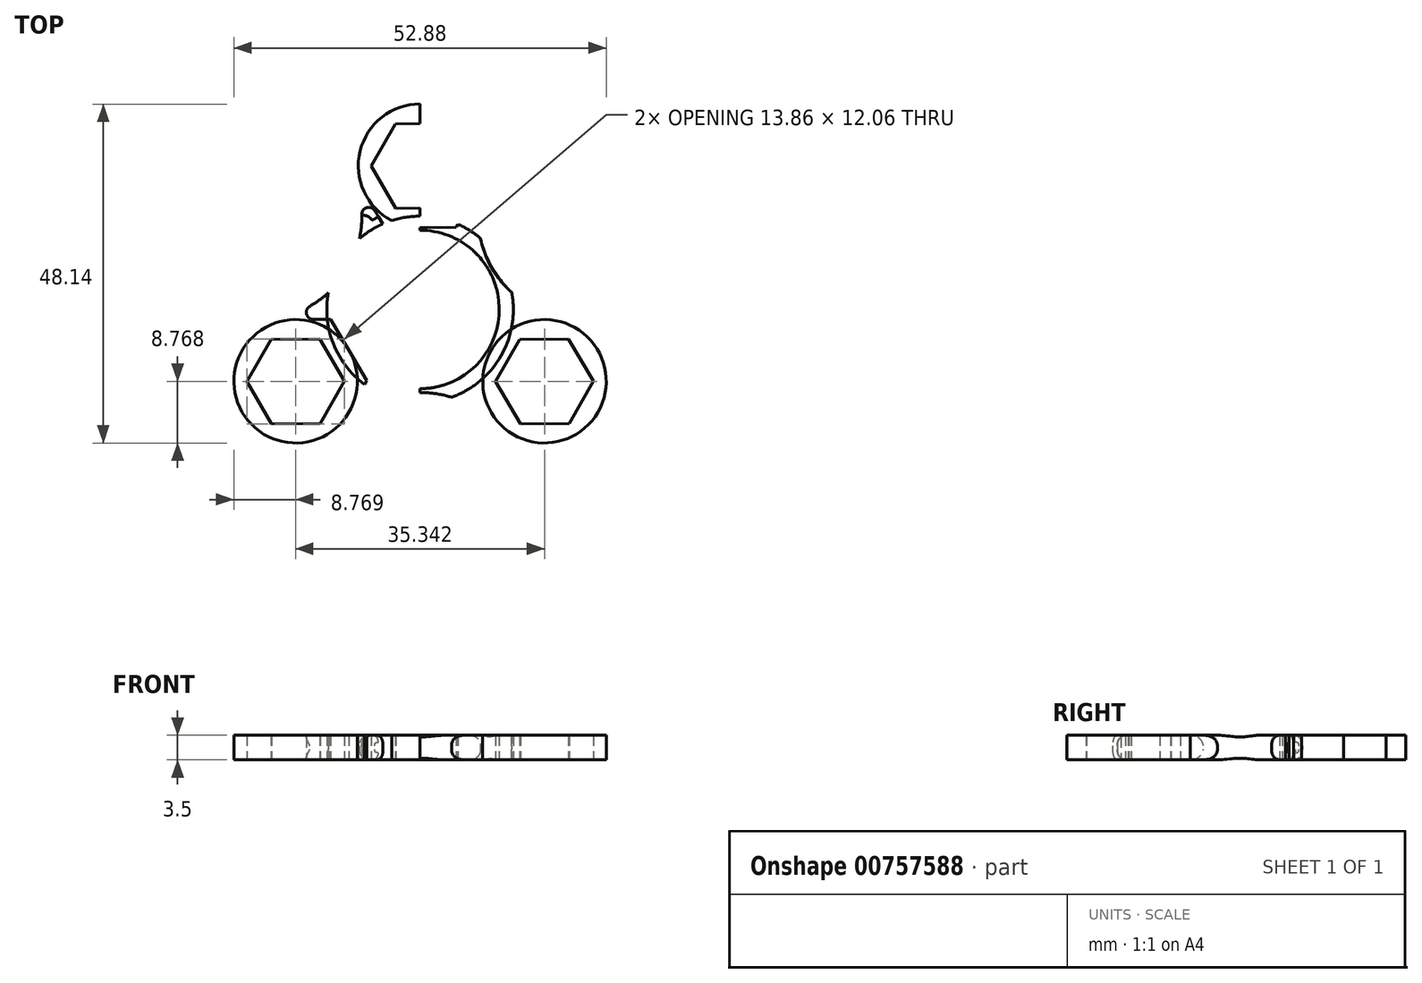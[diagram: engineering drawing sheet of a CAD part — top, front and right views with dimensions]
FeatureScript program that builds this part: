
annotation { "Feature Type Name" : "Feature", "Feature Type Description" : "" }
export const myFeature = defineFeature(function(context is Context, id is Id, definition is map)
    precondition{}
    {
        {
            var Q0;
            Q0=qCreatedBy(makeId("Top.planeOp"),FACE);
            var sketch = newSketch(context, id + "F0", { "sketchPlane" : qUnion([Q0])});
            skCircle(sketch, "E0", {"center": v(0, 0) * mm, "radius": 11.25 * mm});
            skCircle(sketch, "E1", {"center": v(0, 0) * mm, "radius": 13.25 * mm});
            skCircle(sketch, "E2.cCircle", {"center": v(0, 20.4) * mm, "radius": 6 * mm});
            skLineSegment(sketch, "E2.0", {"start": v(-3.52, 26.37) * mm, "end": v(3.41, 26.43) * mm});
            skLineSegment(sketch, "E2.1", {"start": v(3.41, 26.43) * mm, "end": v(6.93, 20.46) * mm});
            skLineSegment(sketch, "E2.2", {"start": v(6.93, 20.46) * mm, "end": v(3.52, 14.43) * mm});
            skLineSegment(sketch, "E2.3", {"start": v(3.52, 14.43) * mm, "end": v(-3.41, 14.38) * mm});
            skLineSegment(sketch, "E2.4", {"start": v(-3.41, 14.38) * mm, "end": v(-6.93, 20.35) * mm});
            skLineSegment(sketch, "E2.5", {"start": v(-6.93, 20.35) * mm, "end": v(-3.52, 26.37) * mm});
            skPoint(sketch, "E2.0.midPoint", {"position": v(-0.05, 26.4) * mm});
            skLineSegment(sketch, "E3", {"start": v(0, 35.27) * mm, "end": v(0, -24.23) * mm});
            skCircle(sketch, "E4.cCircle", {"center": v(0, 20.4) * mm, "radius": 8.77 * mm});
            skLineSegment(sketch, "E4.0", {"start": v(4.99, 29.21) * mm, "end": v(10.12, 20.5) * mm});
            skLineSegment(sketch, "E4.1", {"start": v(10.12, 20.5) * mm, "end": v(5.14, 11.68) * mm});
            skLineSegment(sketch, "E4.2", {"start": v(5.14, 11.68) * mm, "end": v(-4.99, 11.6) * mm});
            skLineSegment(sketch, "E4.3", {"start": v(-4.99, 11.6) * mm, "end": v(-10.12, 20.32) * mm});
            skLineSegment(sketch, "E4.4", {"start": v(-10.12, 20.32) * mm, "end": v(-5.14, 29.13) * mm});
            skLineSegment(sketch, "E4.5", {"start": v(-5.14, 29.13) * mm, "end": v(4.99, 29.21) * mm});
            skPoint(sketch, "E4.0.midPoint", {"position": v(7.56, 24.85) * mm});
            skCircle(sketch, "E5.1.0", {"center": v(-17.67, -10.2) * mm, "radius": 8.77 * mm});
            skCircle(sketch, "E5.1.1", {"center": v(-17.67, -10.2) * mm, "radius": 6 * mm});
            skLineSegment(sketch, "E5.1.2", {"start": v(-21.19, -4.23) * mm, "end": v(-14.26, -4.17) * mm});
            skPoint(sketch, "E5.1.3", {"position": v(-22.84, -13.25) * mm});
            skPoint(sketch, "E5.1.6", {"position": v(-25.3, -5.88) * mm});
            skLineSegment(sketch, "E5.1.7", {"start": v(-7.55, -10.12) * mm, "end": v(-12.53, -18.93) * mm});
            skLineSegment(sketch, "E5.1.8", {"start": v(-12.68, -1.4) * mm, "end": v(-7.55, -10.12) * mm});
            skLineSegment(sketch, "E5.1.9", {"start": v(-14.26, -4.17) * mm, "end": v(-10.74, -10.14) * mm});
            skLineSegment(sketch, "E5.1.10", {"start": v(-10.74, -10.14) * mm, "end": v(-14.16, -16.17) * mm});
            skLineSegment(sketch, "E5.1.11", {"start": v(-22.8, -1.48) * mm, "end": v(-12.68, -1.4) * mm});
            skLineSegment(sketch, "E5.1.12", {"start": v(-22.66, -19.01) * mm, "end": v(-27.8, -10.29) * mm});
            skLineSegment(sketch, "E5.1.13", {"start": v(-21.08, -16.23) * mm, "end": v(-24.6, -10.26) * mm});
            skLineSegment(sketch, "E5.1.14", {"start": v(-24.6, -10.26) * mm, "end": v(-21.19, -4.23) * mm});
            skLineSegment(sketch, "E5.1.15", {"start": v(-14.16, -16.17) * mm, "end": v(-21.08, -16.23) * mm});
            skCircle(sketch, "E5.2.0", {"center": v(17.67, -10.2) * mm, "radius": 8.77 * mm});
            skCircle(sketch, "E5.2.1", {"center": v(17.67, -10.2) * mm, "radius": 6 * mm});
            skLineSegment(sketch, "E5.2.2", {"start": v(14.26, -16.23) * mm, "end": v(10.74, -10.26) * mm});
            skPoint(sketch, "E5.2.3", {"position": v(22.9, -13.16) * mm});
            skPoint(sketch, "E5.2.6", {"position": v(17.75, -18.97) * mm});
            skLineSegment(sketch, "E5.2.7", {"start": v(12.53, -1.48) * mm, "end": v(22.66, -1.4) * mm});
            skLineSegment(sketch, "E5.2.8", {"start": v(7.55, -10.29) * mm, "end": v(12.53, -1.48) * mm});
            skLineSegment(sketch, "E5.2.9", {"start": v(10.74, -10.26) * mm, "end": v(14.16, -4.23) * mm});
            skLineSegment(sketch, "E5.2.10", {"start": v(14.16, -4.23) * mm, "end": v(21.08, -4.17) * mm});
            skLineSegment(sketch, "E5.2.11", {"start": v(12.68, -19.01) * mm, "end": v(7.55, -10.29) * mm});
            skLineSegment(sketch, "E5.2.12", {"start": v(27.8, -10.12) * mm, "end": v(22.8, -18.93) * mm});
            skLineSegment(sketch, "E5.2.13", {"start": v(24.6, -10.14) * mm, "end": v(21.19, -16.17) * mm});
            skLineSegment(sketch, "E5.2.14", {"start": v(21.19, -16.17) * mm, "end": v(14.26, -16.23) * mm});
            skLineSegment(sketch, "E5.2.15", {"start": v(21.08, -4.17) * mm, "end": v(24.6, -10.14) * mm});
            skLineSegment(sketch, "E6", {"start": v(-12.53, -18.93) * mm, "end": v(-22.66, -19.01) * mm});
            skLineSegment(sketch, "E7", {"start": v(-27.8, -10.29) * mm, "end": v(-22.8, -1.48) * mm});
            skLineSegment(sketch, "E8", {"start": v(12.68, -19.01) * mm, "end": v(22.8, -18.93) * mm});
            skLineSegment(sketch, "E9", {"start": v(27.8, -10.12) * mm, "end": v(22.66, -1.4) * mm});
            skArc(sketch, "E10", {"start": v(12.68, -19.01) * mm, "mid": v(0.1, -11.79) * mm, "end": v(-12.53, -18.93) * mm});
            skArc(sketch, "E11.1.0", {"start": v(10.12, 20.5) * mm, "mid": v(10.16, 5.98) * mm, "end": v(22.66, -1.4) * mm});
            skArc(sketch, "E11.2.0", {"start": v(-22.8, -1.48) * mm, "mid": v(-10.26, 5.8) * mm, "end": v(-10.12, 20.32) * mm});
            skSolve(sketch);
        }
        {
            var Q0;
            Q0=makeQuery(id+"F0.imprint","IMPRINT",FACE,{"disambiguationData":[TD([[makeQuery(id+"F0.imprint","IMPRINT",EDGE,{"derivedFrom":sQuery(id+"F0.wireOp",EDGE,"E5.1.2")}),1.0]])]});
            var Q1;
            {var subQ0=sQuery(id+"F0.wireOp",EDGE,"E11.2.0");var subQ3=sQuery(id+"F0.wireOp",EDGE,"E1");var subQ5=makeQuery(id+"F0.imprint","INTERSECT",VERTEX,{"disambiguationData":[OD(1.0)],"derivedFrom":[subQ3,subQ0]});Q1=makeQuery(id+"F0.imprint","IMPRINT",FACE,{"disambiguationData":[TD([[makeQuery(id+"F0.imprint","IMPRINT",EDGE,{"disambiguationData":[TD([[subQ5,-1.0]])],"derivedFrom":subQ3}),-1.0]])]});}
            var Q2;
            {var subQ15=sQuery(id+"F0.wireOp",EDGE,"E4.2");Q2=makeQuery(id+"F0.imprint","IMPRINT",FACE,{"disambiguationData":[TD([[makeQuery(id+"F0.imprint","IMPRINT",EDGE,{"derivedFrom":subQ15}),1.0]])]});}
            var Q3;
            {var subQ0=sQuery(id+"F0.wireOp",EDGE,"E11.2.0");var subQ3=sQuery(id+"F0.wireOp",EDGE,"E1");var subQ5=makeQuery(id+"F0.imprint","INTERSECT",VERTEX,{"disambiguationData":[OD(0.0)],"derivedFrom":[subQ3,subQ0]});Q3=makeQuery(id+"F0.imprint","IMPRINT",FACE,{"disambiguationData":[TD([[makeQuery(id+"F0.imprint","IMPRINT",EDGE,{"disambiguationData":[TD([[subQ5,1.0]])],"derivedFrom":subQ3}),-1.0]])]});}
            var Q4;
            {var subQ0=sQuery(id+"F0.wireOp",EDGE,"E5.1.8");Q4=makeQuery(id+"F0.imprint","IMPRINT",FACE,{"disambiguationData":[TD([[makeQuery(id+"F0.imprint","IMPRINT",EDGE,{"derivedFrom":subQ0}),-1.0]])]});}
            var Q5;
            {var subQ0=sQuery(id+"F0.wireOp",EDGE,"E10");var subQ3=sQuery(id+"F0.wireOp",EDGE,"E1");var subQ5=makeQuery(id+"F0.imprint","INTERSECT",VERTEX,{"disambiguationData":[OD(1.0)],"derivedFrom":[subQ3,subQ0]});Q5=makeQuery(id+"F0.imprint","IMPRINT",FACE,{"disambiguationData":[TD([[makeQuery(id+"F0.imprint","IMPRINT",EDGE,{"disambiguationData":[TD([[subQ5,1.0]])],"derivedFrom":subQ3}),-1.0]])]});}
            var Q6;
            {var subQ0=sQuery(id+"F0.wireOp",EDGE,"E10");var subQ1=sQuery(id+"F0.wireOp",EDGE,"E1");var subQ2=makeQuery(id+"F0.imprint","INTERSECT",VERTEX,{"disambiguationData":[OD(0.0)],"derivedFrom":[subQ1,subQ0]});Q6=makeQuery(id+"F0.imprint","IMPRINT",FACE,{"disambiguationData":[TD([[makeQuery(id+"F0.imprint","IMPRINT",EDGE,{"disambiguationData":[TD([[subQ2,-1.0]])],"derivedFrom":subQ1}),-1.0]])]});}
            var Q7;
            {var subQ5=sQuery(id+"F0.wireOp",EDGE,"E5.2.8");Q7=makeQuery(id+"F0.imprint","IMPRINT",FACE,{"disambiguationData":[TD([[makeQuery(id+"F0.imprint","IMPRINT",EDGE,{"derivedFrom":subQ5}),-1.0]])]});}
            var Q8;
            Q8=makeQuery(id+"F0.imprint","IMPRINT",FACE,{"disambiguationData":[TD([[makeQuery(id+"F0.imprint","IMPRINT",EDGE,{"derivedFrom":sQuery(id+"F0.wireOp",EDGE,"E5.2.2")}),1.0]])]});
            var Q9;
            {var subQ0=sQuery(id+"F0.wireOp",EDGE,"E11.1.0");var subQ1=sQuery(id+"F0.wireOp",EDGE,"E1");var subQ2=makeQuery(id+"F0.imprint","INTERSECT",VERTEX,{"disambiguationData":[OD(0.0)],"derivedFrom":[subQ1,subQ0]});Q9=makeQuery(id+"F0.imprint","IMPRINT",FACE,{"disambiguationData":[TD([[makeQuery(id+"F0.imprint","IMPRINT",EDGE,{"disambiguationData":[TD([[subQ2,1.0]])],"derivedFrom":subQ1}),-1.0]])]});}
            var Q10;
            {var subQ0=sQuery(id+"F0.wireOp",EDGE,"E11.1.0");var subQ3=sQuery(id+"F0.wireOp",EDGE,"E1");var subQ5=makeQuery(id+"F0.imprint","INTERSECT",VERTEX,{"disambiguationData":[OD(1.0)],"derivedFrom":[subQ3,subQ0]});Q10=makeQuery(id+"F0.imprint","IMPRINT",FACE,{"disambiguationData":[TD([[makeQuery(id+"F0.imprint","IMPRINT",EDGE,{"disambiguationData":[TD([[subQ5,-1.0]])],"derivedFrom":subQ3}),-1.0]])]});}
            var Q11;
            {var subQ0=sQuery(id+"F0.wireOp",EDGE,"E4.2");Q11=makeQuery(id+"F0.imprint","IMPRINT",FACE,{"disambiguationData":[TD([[makeQuery(id+"F0.imprint","IMPRINT",EDGE,{"derivedFrom":subQ0}),-1.0]])]});}
            var Q12;
            Q12=makeQuery(id+"F0.imprint","IMPRINT",FACE,{"disambiguationData":[TD([[makeQuery(id+"F0.imprint","IMPRINT",EDGE,{"derivedFrom":sQuery(id+"F0.wireOp",EDGE,"E2.0")}),1.0]])]});
            extrude(context, id + "F1", {"entities" : qUnion([Q0, Q1, Q2, Q3, Q4, Q5, Q6, Q7, Q8, Q9, Q10, Q11, Q12]), "depth" : 3.5 * mm, "offsetDistance" : 25 * mm});
        }
        {
            var Q0;
            Q0=makeQuery(id+"F1.opExtrude","CAP_EDGE",EDGE,{"disambiguationData":[OSD([sQuery(id+"F0.wireOp",EDGE,"E4.5")])],"isStart":false});
            var Q1;
            Q1=makeQuery(id+"F1.opExtrude","CAP_EDGE",EDGE,{"disambiguationData":[OSD([sQuery(id+"F0.wireOp",EDGE,"E11.2.0")])],"isStart":false});
            var Q2;
            Q2=makeQuery(id+"F1.opExtrude","CAP_EDGE",EDGE,{"disambiguationData":[OSD([sQuery(id+"F0.wireOp",EDGE,"E4.4")])],"isStart":false});
            var Q3;
            Q3=makeQuery(id+"F1.opExtrude","CAP_EDGE",EDGE,{"disambiguationData":[OSD([sQuery(id+"F0.wireOp",EDGE,"E7")])],"isStart":false});
            var Q4;
            Q4=makeQuery(id+"F1.opExtrude","CAP_EDGE",EDGE,{"disambiguationData":[OSD([sQuery(id+"F0.wireOp",EDGE,"E5.1.12")])],"isStart":false});
            var Q5;
            Q5=makeQuery(id+"F1.opExtrude","CAP_EDGE",EDGE,{"disambiguationData":[OSD([sQuery(id+"F0.wireOp",EDGE,"E6")])],"isStart":false});
            var Q6;
            Q6=makeQuery(id+"F1.opExtrude","CAP_EDGE",EDGE,{"disambiguationData":[OSD([sQuery(id+"F0.wireOp",EDGE,"E10")])],"isStart":false});
            var Q7;
            Q7=makeQuery(id+"F1.opExtrude","CAP_EDGE",EDGE,{"disambiguationData":[OSD([sQuery(id+"F0.wireOp",EDGE,"E8")])],"isStart":false});
            var Q8;
            Q8=makeQuery(id+"F1.opExtrude","CAP_EDGE",EDGE,{"disambiguationData":[OSD([sQuery(id+"F0.wireOp",EDGE,"E9")])],"isStart":false});
            var Q9;
            Q9=makeQuery(id+"F1.opExtrude","CAP_EDGE",EDGE,{"disambiguationData":[OSD([sQuery(id+"F0.wireOp",EDGE,"E11.1.0")])],"isStart":false});
            var Q10;
            Q10=makeQuery(id+"F1.opExtrude","CAP_EDGE",EDGE,{"disambiguationData":[OSD([sQuery(id+"F0.wireOp",EDGE,"E6")])],"isStart":true});
            var Q11;
            Q11=makeQuery(id+"F1.opExtrude","CAP_EDGE",EDGE,{"disambiguationData":[OSD([sQuery(id+"F0.wireOp",EDGE,"E10")])],"isStart":true});
            var Q12;
            Q12=makeQuery(id+"F1.opExtrude","CAP_EDGE",EDGE,{"disambiguationData":[OSD([sQuery(id+"F0.wireOp",EDGE,"E5.1.12")])],"isStart":true});
            var Q13;
            Q13=makeQuery(id+"F1.opExtrude","CAP_EDGE",EDGE,{"disambiguationData":[OSD([sQuery(id+"F0.wireOp",EDGE,"E7")])],"isStart":true});
            var Q14;
            Q14=makeQuery(id+"F1.opExtrude","CAP_EDGE",EDGE,{"disambiguationData":[OSD([sQuery(id+"F0.wireOp",EDGE,"E11.2.0")])],"isStart":true});
            var Q15;
            Q15=makeQuery(id+"F1.opExtrude","CAP_EDGE",EDGE,{"disambiguationData":[OSD([sQuery(id+"F0.wireOp",EDGE,"E4.4")])],"isStart":true});
            var Q16;
            Q16=makeQuery(id+"F1.opExtrude","CAP_EDGE",EDGE,{"disambiguationData":[OSD([sQuery(id+"F0.wireOp",EDGE,"E4.5")])],"isStart":true});
            var Q17;
            Q17=makeQuery(id+"F1.opExtrude","CAP_EDGE",EDGE,{"disambiguationData":[OSD([sQuery(id+"F0.wireOp",EDGE,"E4.0")])],"isStart":false});
            var Q18;
            Q18=makeQuery(id+"F1.opExtrude","CAP_EDGE",EDGE,{"disambiguationData":[OSD([sQuery(id+"F0.wireOp",EDGE,"E4.0")])],"isStart":true});
            var Q19;
            Q19=makeQuery(id+"F1.opExtrude","CAP_EDGE",EDGE,{"disambiguationData":[OSD([sQuery(id+"F0.wireOp",EDGE,"E11.1.0")])],"isStart":true});
            var Q20;
            Q20=makeQuery(id+"F1.opExtrude","CAP_EDGE",EDGE,{"disambiguationData":[OSD([sQuery(id+"F0.wireOp",EDGE,"E9")])],"isStart":true});
            var Q21;
            Q21=makeQuery(id+"F1.opExtrude","CAP_EDGE",EDGE,{"disambiguationData":[OSD([sQuery(id+"F0.wireOp",EDGE,"E5.2.12")])],"isStart":true});
            var Q22;
            Q22=makeQuery(id+"F1.opExtrude","CAP_EDGE",EDGE,{"disambiguationData":[OSD([sQuery(id+"F0.wireOp",EDGE,"E8")])],"isStart":true});
            fillet(context, id + "F2", {"entities" : qUnion([Q0, Q1, Q2, Q3, Q4, Q5, Q6, Q7, Q8, Q9, Q10, Q11, Q12, Q13, Q14, Q15, Q16, Q17, Q18, Q19, Q20, Q21, Q22]), "radius" : 1.5 * mm, "tangentPropagation" : true, "rho" : 0.5, "crossSection" : FilletCrossSection.CONIC, "allowEdgeOverflow" : false});
        }
        {
            var Q0;
            Q0=makeQuery(id+"F2.opFillet","BLEND_EDGE",EDGE,{"blendedFrom":[makeQuery(id+"F1.opExtrude","CAP_EDGE",EDGE,{"disambiguationData":[OSD([sQuery(id+"F0.wireOp",EDGE,"E9")])],"isStart":false}),makeQuery(id+"F1.opExtrude","CAP_EDGE",EDGE,{"disambiguationData":[OSD([sQuery(id+"F0.wireOp",EDGE,"E11.1.0")])],"isStart":false})],"blendedInto":[]});
            var Q1;
            Q1=makeQuery(id+"F2.opFillet","BLEND_EDGE",EDGE,{"blendedFrom":[makeQuery(id+"F1.opExtrude","CAP_EDGE",EDGE,{"disambiguationData":[OSD([sQuery(id+"F0.wireOp",EDGE,"E9")])],"isStart":true}),makeQuery(id+"F1.opExtrude","CAP_EDGE",EDGE,{"disambiguationData":[OSD([sQuery(id+"F0.wireOp",EDGE,"E11.1.0")])],"isStart":true})],"blendedInto":[]});
            var Q2;
            Q2=makeQuery(id+"F2.opFillet","BLEND_EDGE",EDGE,{"blendedFrom":[makeQuery(id+"F1.opExtrude","CAP_EDGE",EDGE,{"disambiguationData":[OSD([sQuery(id+"F0.wireOp",EDGE,"E8")])],"isStart":false}),makeQuery(id+"F1.opExtrude","CAP_EDGE",EDGE,{"disambiguationData":[OSD([sQuery(id+"F0.wireOp",EDGE,"E10")])],"isStart":false})],"blendedInto":[]});
            var Q3;
            Q3=makeQuery(id+"F2.opFillet","BLEND_EDGE",EDGE,{"blendedFrom":[makeQuery(id+"F1.opExtrude","CAP_EDGE",EDGE,{"disambiguationData":[OSD([sQuery(id+"F0.wireOp",EDGE,"E8")])],"isStart":true}),makeQuery(id+"F1.opExtrude","CAP_EDGE",EDGE,{"disambiguationData":[OSD([sQuery(id+"F0.wireOp",EDGE,"E10")])],"isStart":true})],"blendedInto":[]});
            var Q4;
            Q4=makeQuery(id+"F1.opExtrude","SWEPT_EDGE",EDGE,{"disambiguationData":[OSD([sQuery(id+"F0.wireOp",EDGE,"E5.2.11"),sQuery(id+"F0.wireOp",EDGE,"E8"),sQuery(id+"F0.wireOp",EDGE,"E10")])]});
            var Q5;
            Q5=makeQuery(id+"F2.opFillet","BLEND_EDGE",EDGE,{"blendedFrom":[makeQuery(id+"F1.opExtrude","CAP_EDGE",EDGE,{"disambiguationData":[OSD([sQuery(id+"F0.wireOp",EDGE,"E6")])],"isStart":false}),makeQuery(id+"F1.opExtrude","CAP_EDGE",EDGE,{"disambiguationData":[OSD([sQuery(id+"F0.wireOp",EDGE,"E10")])],"isStart":false})],"blendedInto":[]});
            var Q6;
            Q6=makeQuery(id+"F1.opExtrude","SWEPT_EDGE",EDGE,{"disambiguationData":[OSD([sQuery(id+"F0.wireOp",EDGE,"E5.1.7"),sQuery(id+"F0.wireOp",EDGE,"E6"),sQuery(id+"F0.wireOp",EDGE,"E10")])]});
            var Q7;
            Q7=makeQuery(id+"F2.opFillet","BLEND_EDGE",EDGE,{"blendedFrom":[makeQuery(id+"F1.opExtrude","CAP_EDGE",EDGE,{"disambiguationData":[OSD([sQuery(id+"F0.wireOp",EDGE,"E6")])],"isStart":true}),makeQuery(id+"F1.opExtrude","CAP_EDGE",EDGE,{"disambiguationData":[OSD([sQuery(id+"F0.wireOp",EDGE,"E10")])],"isStart":true})],"blendedInto":[]});
            var Q8;
            Q8=makeQuery(id+"F2.opFillet","BLEND_EDGE",EDGE,{"blendedFrom":[makeQuery(id+"F1.opExtrude","CAP_EDGE",EDGE,{"disambiguationData":[OSD([sQuery(id+"F0.wireOp",EDGE,"E5.1.12")])],"isStart":false}),makeQuery(id+"F1.opExtrude","CAP_EDGE",EDGE,{"disambiguationData":[OSD([sQuery(id+"F0.wireOp",EDGE,"E6")])],"isStart":false})],"blendedInto":[]});
            var Q9;
            Q9=makeQuery(id+"F1.opExtrude","SWEPT_EDGE",EDGE,{"disambiguationData":[OSD([sQuery(id+"F0.wireOp",EDGE,"E5.1.12"),sQuery(id+"F0.wireOp",EDGE,"E6")])]});
            var Q10;
            Q10=makeQuery(id+"F2.opFillet","BLEND_EDGE",EDGE,{"blendedFrom":[makeQuery(id+"F1.opExtrude","CAP_EDGE",EDGE,{"disambiguationData":[OSD([sQuery(id+"F0.wireOp",EDGE,"E5.1.12")])],"isStart":true}),makeQuery(id+"F1.opExtrude","CAP_EDGE",EDGE,{"disambiguationData":[OSD([sQuery(id+"F0.wireOp",EDGE,"E6")])],"isStart":true})],"blendedInto":[]});
            var Q11;
            Q11=makeQuery(id+"F2.opFillet","BLEND_EDGE",EDGE,{"blendedFrom":[makeQuery(id+"F1.opExtrude","CAP_EDGE",EDGE,{"disambiguationData":[OSD([sQuery(id+"F0.wireOp",EDGE,"E5.1.12")])],"isStart":false}),makeQuery(id+"F1.opExtrude","CAP_EDGE",EDGE,{"disambiguationData":[OSD([sQuery(id+"F0.wireOp",EDGE,"E7")])],"isStart":false})],"blendedInto":[]});
            var Q12;
            Q12=makeQuery(id+"F1.opExtrude","SWEPT_EDGE",EDGE,{"disambiguationData":[OSD([sQuery(id+"F0.wireOp",EDGE,"E5.1.12"),sQuery(id+"F0.wireOp",EDGE,"E7")])]});
            var Q13;
            Q13=makeQuery(id+"F2.opFillet","BLEND_EDGE",EDGE,{"blendedFrom":[makeQuery(id+"F1.opExtrude","CAP_EDGE",EDGE,{"disambiguationData":[OSD([sQuery(id+"F0.wireOp",EDGE,"E5.1.12")])],"isStart":true}),makeQuery(id+"F1.opExtrude","CAP_EDGE",EDGE,{"disambiguationData":[OSD([sQuery(id+"F0.wireOp",EDGE,"E7")])],"isStart":true})],"blendedInto":[]});
            var Q14;
            Q14=makeQuery(id+"F2.opFillet","BLEND_EDGE",EDGE,{"blendedFrom":[makeQuery(id+"F1.opExtrude","CAP_EDGE",EDGE,{"disambiguationData":[OSD([sQuery(id+"F0.wireOp",EDGE,"E7")])],"isStart":false}),makeQuery(id+"F1.opExtrude","CAP_EDGE",EDGE,{"disambiguationData":[OSD([sQuery(id+"F0.wireOp",EDGE,"E11.2.0")])],"isStart":false})],"blendedInto":[]});
            var Q15;
            Q15=makeQuery(id+"F1.opExtrude","SWEPT_EDGE",EDGE,{"disambiguationData":[OSD([sQuery(id+"F0.wireOp",EDGE,"E5.1.11"),sQuery(id+"F0.wireOp",EDGE,"E7"),sQuery(id+"F0.wireOp",EDGE,"E11.2.0")])]});
            var Q16;
            Q16=makeQuery(id+"F2.opFillet","BLEND_EDGE",EDGE,{"blendedFrom":[makeQuery(id+"F1.opExtrude","CAP_EDGE",EDGE,{"disambiguationData":[OSD([sQuery(id+"F0.wireOp",EDGE,"E7")])],"isStart":true}),makeQuery(id+"F1.opExtrude","CAP_EDGE",EDGE,{"disambiguationData":[OSD([sQuery(id+"F0.wireOp",EDGE,"E11.2.0")])],"isStart":true})],"blendedInto":[]});
            var Q17;
            Q17=makeQuery(id+"F2.opFillet","BLEND_EDGE",EDGE,{"blendedFrom":[makeQuery(id+"F1.opExtrude","CAP_EDGE",EDGE,{"disambiguationData":[OSD([sQuery(id+"F0.wireOp",EDGE,"E4.4")])],"isStart":false}),makeQuery(id+"F1.opExtrude","CAP_EDGE",EDGE,{"disambiguationData":[OSD([sQuery(id+"F0.wireOp",EDGE,"E11.2.0")])],"isStart":false})],"blendedInto":[]});
            var Q18;
            Q18=makeQuery(id+"F2.opFillet","BLEND_EDGE",EDGE,{"blendedFrom":[makeQuery(id+"F1.opExtrude","CAP_EDGE",EDGE,{"disambiguationData":[OSD([sQuery(id+"F0.wireOp",EDGE,"E4.4")])],"isStart":true}),makeQuery(id+"F1.opExtrude","CAP_EDGE",EDGE,{"disambiguationData":[OSD([sQuery(id+"F0.wireOp",EDGE,"E11.2.0")])],"isStart":true})],"blendedInto":[]});
            var Q19;
            Q19=makeQuery(id+"F1.opExtrude","SWEPT_EDGE",EDGE,{"disambiguationData":[OSD([sQuery(id+"F0.wireOp",EDGE,"E4.3"),sQuery(id+"F0.wireOp",EDGE,"E4.4"),sQuery(id+"F0.wireOp",EDGE,"E11.2.0")])]});
            var Q20;
            Q20=makeQuery(id+"F2.opFillet","BLEND_EDGE",EDGE,{"blendedFrom":[makeQuery(id+"F1.opExtrude","CAP_EDGE",EDGE,{"disambiguationData":[OSD([sQuery(id+"F0.wireOp",EDGE,"E4.4")])],"isStart":false}),makeQuery(id+"F1.opExtrude","CAP_EDGE",EDGE,{"disambiguationData":[OSD([sQuery(id+"F0.wireOp",EDGE,"E4.5")])],"isStart":false})],"blendedInto":[]});
            var Q21;
            Q21=makeQuery(id+"F1.opExtrude","SWEPT_EDGE",EDGE,{"disambiguationData":[OSD([sQuery(id+"F0.wireOp",EDGE,"E4.4"),sQuery(id+"F0.wireOp",EDGE,"E4.5")])]});
            var Q22;
            Q22=makeQuery(id+"F2.opFillet","BLEND_EDGE",EDGE,{"blendedFrom":[makeQuery(id+"F1.opExtrude","CAP_EDGE",EDGE,{"disambiguationData":[OSD([sQuery(id+"F0.wireOp",EDGE,"E4.4")])],"isStart":true}),makeQuery(id+"F1.opExtrude","CAP_EDGE",EDGE,{"disambiguationData":[OSD([sQuery(id+"F0.wireOp",EDGE,"E4.5")])],"isStart":true})],"blendedInto":[]});
            var Q23;
            Q23=makeQuery(id+"F2.opFillet","BLEND_EDGE",EDGE,{"blendedFrom":[makeQuery(id+"F1.opExtrude","CAP_EDGE",EDGE,{"disambiguationData":[OSD([sQuery(id+"F0.wireOp",EDGE,"E4.0")])],"isStart":false}),makeQuery(id+"F1.opExtrude","CAP_EDGE",EDGE,{"disambiguationData":[OSD([sQuery(id+"F0.wireOp",EDGE,"E4.5")])],"isStart":false})],"blendedInto":[]});
            var Q24;
            Q24=makeQuery(id+"F1.opExtrude","SWEPT_EDGE",EDGE,{"disambiguationData":[OSD([sQuery(id+"F0.wireOp",EDGE,"E4.0"),sQuery(id+"F0.wireOp",EDGE,"E4.5")])]});
            var Q25;
            Q25=makeQuery(id+"F2.opFillet","BLEND_EDGE",EDGE,{"blendedFrom":[makeQuery(id+"F1.opExtrude","CAP_EDGE",EDGE,{"disambiguationData":[OSD([sQuery(id+"F0.wireOp",EDGE,"E4.0")])],"isStart":true}),makeQuery(id+"F1.opExtrude","CAP_EDGE",EDGE,{"disambiguationData":[OSD([sQuery(id+"F0.wireOp",EDGE,"E4.5")])],"isStart":true})],"blendedInto":[]});
            var Q26;
            Q26=makeQuery(id+"F2.opFillet","BLEND_EDGE",EDGE,{"blendedFrom":[makeQuery(id+"F1.opExtrude","CAP_EDGE",EDGE,{"disambiguationData":[OSD([sQuery(id+"F0.wireOp",EDGE,"E4.0")])],"isStart":false}),makeQuery(id+"F1.opExtrude","CAP_EDGE",EDGE,{"disambiguationData":[OSD([sQuery(id+"F0.wireOp",EDGE,"E11.1.0")])],"isStart":false})],"blendedInto":[]});
            var Q27;
            Q27=makeQuery(id+"F1.opExtrude","SWEPT_EDGE",EDGE,{"disambiguationData":[OSD([sQuery(id+"F0.wireOp",EDGE,"E4.0"),sQuery(id+"F0.wireOp",EDGE,"E4.1"),sQuery(id+"F0.wireOp",EDGE,"E11.1.0")])]});
            var Q28;
            Q28=makeQuery(id+"F2.opFillet","BLEND_EDGE",EDGE,{"blendedFrom":[makeQuery(id+"F1.opExtrude","CAP_EDGE",EDGE,{"disambiguationData":[OSD([sQuery(id+"F0.wireOp",EDGE,"E4.0")])],"isStart":true}),makeQuery(id+"F1.opExtrude","CAP_EDGE",EDGE,{"disambiguationData":[OSD([sQuery(id+"F0.wireOp",EDGE,"E11.1.0")])],"isStart":true})],"blendedInto":[]});
            var Q29;
            Q29=makeQuery(id+"F1.opExtrude","SWEPT_EDGE",EDGE,{"disambiguationData":[OSD([sQuery(id+"F0.wireOp",EDGE,"E5.2.7"),sQuery(id+"F0.wireOp",EDGE,"E9"),sQuery(id+"F0.wireOp",EDGE,"E11.1.0")])]});
            var Q30;
            {var subQ0=sQuery(id+"F0.wireOp",EDGE,"E9");Q30=makeQuery(id+"F2.opFillet","BLEND_FACE",FACE,{"disambiguationData":[OSD([subQ0]),TDD([makeQuery(id+"F1.opExtrude","CAP_EDGE",EDGE,{"disambiguationData":[OSD([subQ0])],"isStart":false})])]});}
            var Q31;
            Q31=makeQuery(id+"F1.opExtrude","SWEPT_EDGE",EDGE,{"disambiguationData":[OSD([sQuery(id+"F0.wireOp",EDGE,"E5.2.12"),sQuery(id+"F0.wireOp",EDGE,"E9")])]});
            var Q32;
            Q32=makeQuery(id+"F2.opFillet","BLEND_EDGE",EDGE,{"blendedFrom":[makeQuery(id+"F1.opExtrude","CAP_EDGE",EDGE,{"disambiguationData":[OSD([sQuery(id+"F0.wireOp",EDGE,"E5.2.12")])],"isStart":true}),makeQuery(id+"F1.opExtrude","CAP_EDGE",EDGE,{"disambiguationData":[OSD([sQuery(id+"F0.wireOp",EDGE,"E9")])],"isStart":true})],"blendedInto":[]});
            var Q33;
            Q33=makeQuery(id+"F2.opFillet","BLEND_EDGE",EDGE,{"blendedFrom":[makeQuery(id+"F1.opExtrude","CAP_EDGE",EDGE,{"disambiguationData":[OSD([sQuery(id+"F0.wireOp",EDGE,"E8")])],"isStart":false}),makeQuery(id+"F1.opExtrude","SWEPT_FACE",FACE,{"disambiguationData":[OSD([sQuery(id+"F0.wireOp",EDGE,"E5.2.12")])]})],"blendedInto":[makeQuery(id+"F1.opExtrude","SWEPT_FACE",FACE,{"disambiguationData":[OSD([sQuery(id+"F0.wireOp",EDGE,"E5.2.12")])]})]});
            var Q34;
            Q34=makeQuery(id+"F1.opExtrude","SWEPT_EDGE",EDGE,{"disambiguationData":[OSD([sQuery(id+"F0.wireOp",EDGE,"E5.2.12"),sQuery(id+"F0.wireOp",EDGE,"E8")])]});
            var Q35;
            Q35=makeQuery(id+"F2.opFillet","BLEND_EDGE",EDGE,{"blendedFrom":[makeQuery(id+"F1.opExtrude","CAP_EDGE",EDGE,{"disambiguationData":[OSD([sQuery(id+"F0.wireOp",EDGE,"E5.2.12")])],"isStart":true}),makeQuery(id+"F1.opExtrude","CAP_EDGE",EDGE,{"disambiguationData":[OSD([sQuery(id+"F0.wireOp",EDGE,"E8")])],"isStart":true})],"blendedInto":[]});
            fillet(context, id + "F3", {"entities" : qUnion([Q0, Q1, Q2, Q3, Q4, Q5, Q6, Q7, Q8, Q9, Q10, Q11, Q12, Q13, Q14, Q15, Q16, Q17, Q18, Q19, Q20, Q21, Q22, Q23, Q24, Q25, Q26, Q27, Q28, Q29, Q30, Q31, Q32, Q33, Q34, Q35]), "radius" : 1 * mm, "tangentPropagation" : true, "allowEdgeOverflow" : false});
        }
    });
